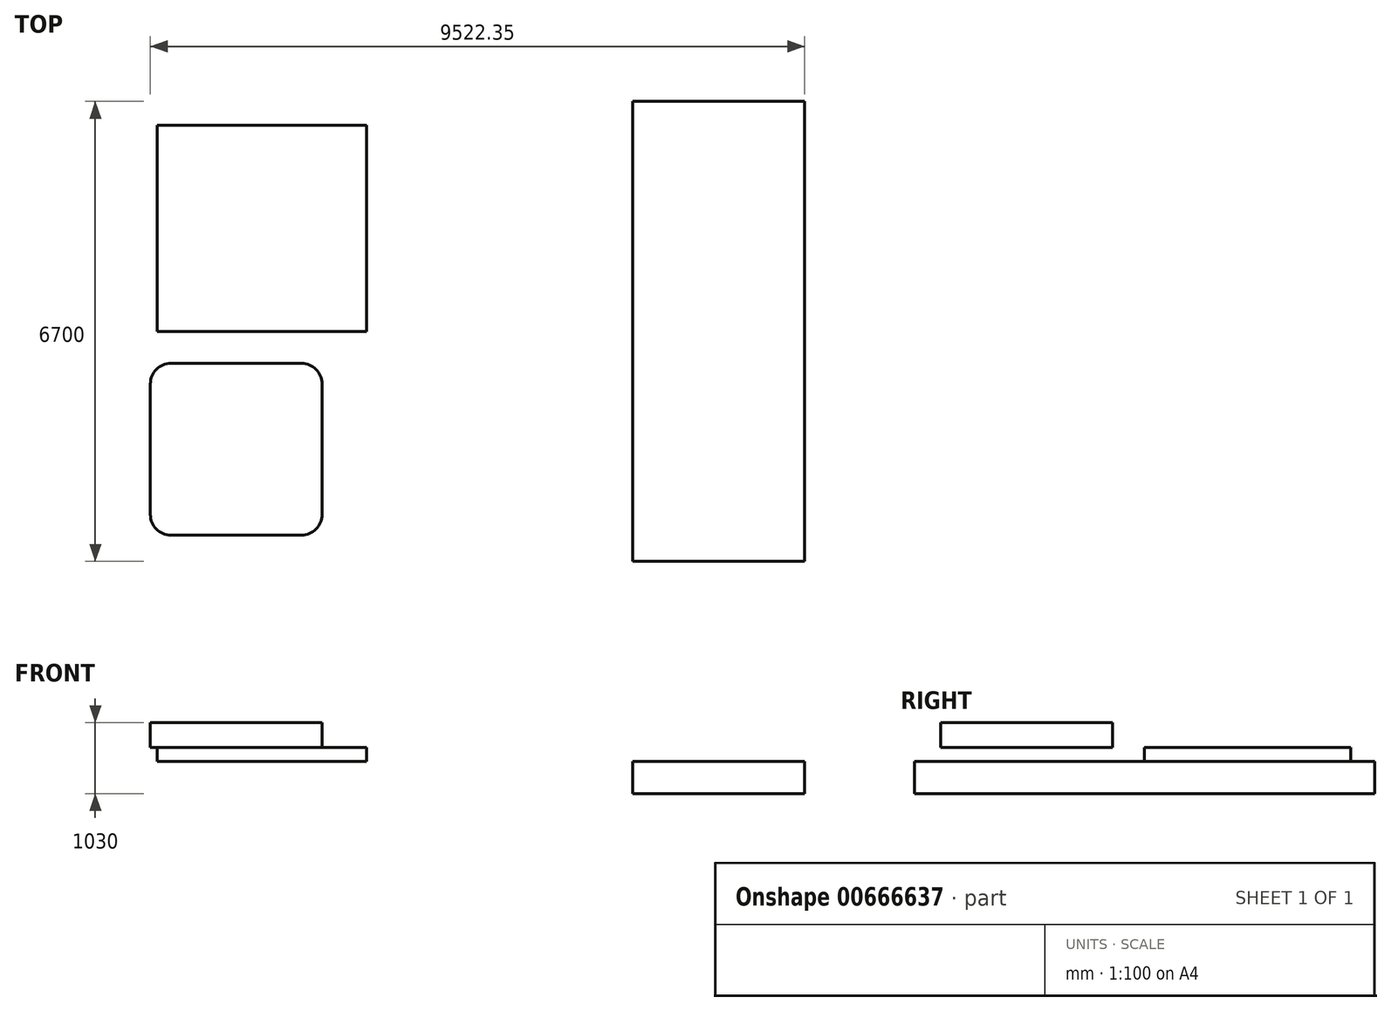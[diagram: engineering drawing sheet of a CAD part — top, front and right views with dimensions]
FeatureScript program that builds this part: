
annotation { "Feature Type Name" : "Feature", "Feature Type Description" : "" }
export const myFeature = defineFeature(function(context is Context, id is Id, definition is map)
    precondition{}
    {
        {
            var Q0;
            Q0=qCreatedBy(makeId("Top.planeOp"),FACE);
            var sketch = newSketch(context, id + "F0", { "sketchPlane" : qUnion([Q0])});
            skLineSegment(sketch, "E0.bottom", {"start": v(1250, -3350) * mm, "end": v(-1250, -3350) * mm});
            skLineSegment(sketch, "E0.top", {"start": v(1250, 3350) * mm, "end": v(-1250, 3350) * mm});
            skLineSegment(sketch, "E0.left", {"start": v(1250, -3350) * mm, "end": v(1250, 3350) * mm});
            skLineSegment(sketch, "E0.right", {"start": v(-1250, -3350) * mm, "end": v(-1250, 3350) * mm});
            skPoint(sketch, "E0.middle", {"position": v(0, 0) * mm});
            skSolve(sketch);
        }
        {
            var Q0;
            Q0=makeQuery(id+"F0.imprint","IMPRINT",FACE,{"disambiguationData":[TD([[makeQuery(id+"F0.imprint","IMPRINT",EDGE,{"derivedFrom":sQuery(id+"F0.wireOp",EDGE,"E0.bottom")}),-1.0]])]});
            extrude(context, id + "F1", {"entities" : qUnion([Q0]), "depth" : 470 * mm, "offsetDistance" : 25 * mm});
        }
        {
            var Q0;
            Q0=makeQuery(id+"F1.opExtrude","CAP_FACE",FACE,{"disambiguationData":[OSD([sQuery(id+"F0.wireOp",EDGE,"E0.bottom"),sQuery(id+"F0.wireOp",EDGE,"E0.top"),sQuery(id+"F0.wireOp",EDGE,"E0.left"),sQuery(id+"F0.wireOp",EDGE,"E0.right")])],"isStart":false});
            var sketch = newSketch(context, id + "F2", { "sketchPlane" : qUnion([Q0])});
            skLineSegment(sketch, "E1.bottom", {"start": v(-5125.17, 0) * mm, "end": v(-8175.17, 0) * mm});
            skLineSegment(sketch, "E1.top", {"start": v(-5125.17, 3000) * mm, "end": v(-8175.17, 3000) * mm});
            skLineSegment(sketch, "E1.left", {"start": v(-5125.17, 0) * mm, "end": v(-5125.17, 3000) * mm});
            skLineSegment(sketch, "E1.right", {"start": v(-8175.17, 0) * mm, "end": v(-8175.17, 3000) * mm});
            skPoint(sketch, "E1.middle", {"position": v(-6650.17, 1500) * mm});
            skSolve(sketch);
        }
        {
            var Q0;
            Q0=makeQuery(id+"F2.imprint","IMPRINT",FACE,{"disambiguationData":[TD([[makeQuery(id+"F2.imprint","IMPRINT",EDGE,{"derivedFrom":sQuery(id+"F2.wireOp",EDGE,"E1.bottom")}),-1.0]])]});
            extrude(context, id + "F3", {"entities" : qUnion([Q0]), "depth" : 200 * mm, "offsetDistance" : 25 * mm});
        }
        {
            var Q0;
            Q0=makeQuery(id+"F3.opExtrude","CAP_FACE",FACE,{"disambiguationData":[OSD([sQuery(id+"F2.wireOp",EDGE,"E1.bottom"),sQuery(id+"F2.wireOp",EDGE,"E1.top"),sQuery(id+"F2.wireOp",EDGE,"E1.left"),sQuery(id+"F2.wireOp",EDGE,"E1.right")])],"isStart":false});
            var sketch = newSketch(context, id + "F4", { "sketchPlane" : qUnion([Q0])});
            skLineSegment(sketch, "E2.bottom", {"start": v(-6072.35, -2965.87) * mm, "end": v(-7972.35, -2965.87) * mm});
            skLineSegment(sketch, "E2.top", {"start": v(-6072.35, -465.87) * mm, "end": v(-7972.35, -465.87) * mm});
            skLineSegment(sketch, "E2.left", {"start": v(-5772.35, -2665.87) * mm, "end": v(-5772.35, -765.87) * mm});
            skLineSegment(sketch, "E2.right", {"start": v(-8272.35, -2665.87) * mm, "end": v(-8272.35, -765.87) * mm});
            skPoint(sketch, "E2.middle", {"position": v(-7022.35, -1715.87) * mm});
            skPoint(sketch, "E3.visualSharp", {"position": v(-8272.35, -465.87) * mm});
            skArc(sketch, "E3.filletArc", {"start": v(-7972.35, -465.87) * mm, "mid": v(-8184.49, -553.74) * mm, "end": v(-8272.35, -765.87) * mm});
            skPoint(sketch, "E4.visualSharp", {"position": v(-5772.35, -465.87) * mm});
            skArc(sketch, "E4.filletArc", {"start": v(-5772.35, -765.87) * mm, "mid": v(-5860.22, -553.74) * mm, "end": v(-6072.35, -465.87) * mm});
            skPoint(sketch, "E5.visualSharp", {"position": v(-5772.35, -2965.87) * mm});
            skArc(sketch, "E5.filletArc", {"start": v(-6072.35, -2965.87) * mm, "mid": v(-5860.22, -2878) * mm, "end": v(-5772.35, -2665.87) * mm});
            skPoint(sketch, "E6.visualSharp", {"position": v(-8272.35, -2965.87) * mm});
            skArc(sketch, "E6.filletArc", {"start": v(-8272.35, -2665.87) * mm, "mid": v(-8184.49, -2878) * mm, "end": v(-7972.35, -2965.87) * mm});
            skSolve(sketch);
        }
        {
            var Q0;
            Q0=makeQuery(id+"F4.imprint","IMPRINT",FACE,{"disambiguationData":[TD([[makeQuery(id+"F4.imprint","IMPRINT",EDGE,{"derivedFrom":sQuery(id+"F4.wireOp",EDGE,"E2.bottom")}),-1.0]])]});
            extrude(context, id + "F5", {"entities" : qUnion([Q0]), "depth" : 360 * mm, "offsetDistance" : 25 * mm});
        }
    });
